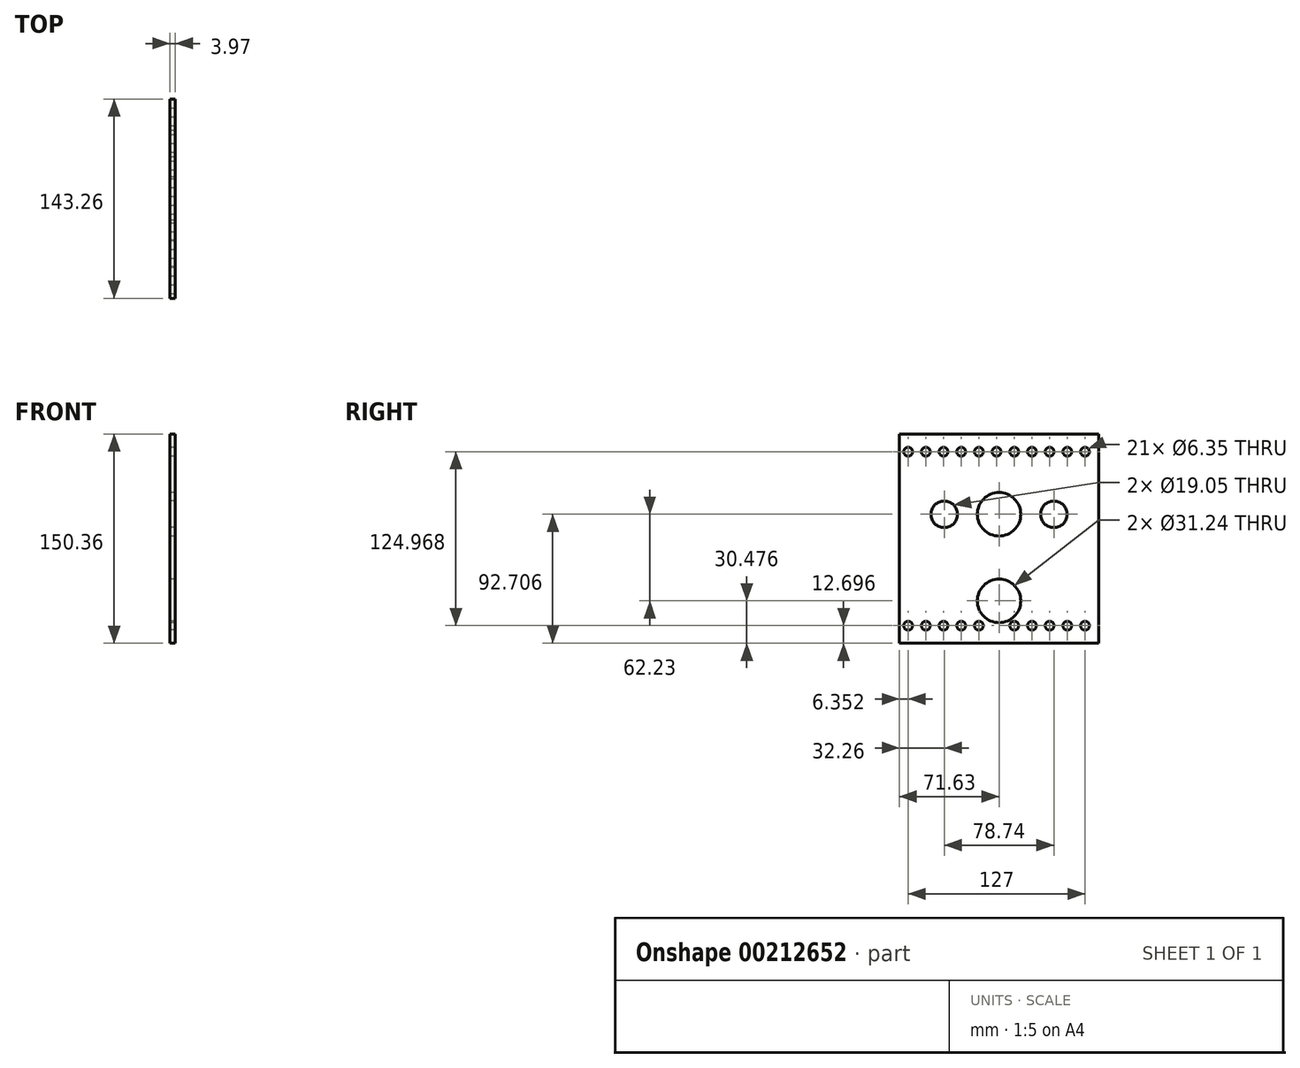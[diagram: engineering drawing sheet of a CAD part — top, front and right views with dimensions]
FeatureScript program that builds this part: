
annotation { "Feature Type Name" : "Feature", "Feature Type Description" : "" }
export const myFeature = defineFeature(function(context is Context, id is Id, definition is map)
    precondition{}
    {
        {
            var Q0;
            Q0=qCreatedBy(makeId("Right.planeOp"),FACE);
            var sketch = newSketch(context, id + "F0", { "sketchPlane" : qUnion([Q0])});
            skLineSegment(sketch, "E0.bottom", {"start": v(71.63, 75.18) * mm, "end": v(-71.63, 75.18) * mm});
            skLineSegment(sketch, "E0.top", {"start": v(71.63, -75.18) * mm, "end": v(-71.63, -75.18) * mm});
            skLineSegment(sketch, "E0.left", {"start": v(71.63, 75.18) * mm, "end": v(71.63, -75.18) * mm});
            skLineSegment(sketch, "E0.right", {"start": v(-71.63, 75.18) * mm, "end": v(-71.63, -75.18) * mm});
            skPoint(sketch, "E0.middle", {"position": v(0, 0) * mm});
            skLineSegment(sketch, "E1", {"start": v(-71.63, 49.78) * mm, "end": v(71.63, 49.78) * mm, "construction": true});
            skLineSegment(sketch, "E2", {"start": v(-71.63, -49.78) * mm, "end": v(71.63, -49.78) * mm, "construction": true});
            skCircle(sketch, "E3", {"center": v(-39.37, 17.53) * mm, "radius": 7.62 * mm, "construction": true});
            skCircle(sketch, "E4", {"center": v(39.37, 17.53) * mm, "radius": 7.62 * mm, "construction": true});
            skLineSegment(sketch, "E5", {"start": v(-39.37, 17.53) * mm, "end": v(-71.63, 17.53) * mm, "construction": true});
            skLineSegment(sketch, "E6", {"start": v(39.37, 17.53) * mm, "end": v(71.63, 17.53) * mm, "construction": true});
            skCircle(sketch, "E7", {"center": v(0, 17.53) * mm, "radius": 31.75 * mm, "construction": true});
            skCircle(sketch, "E8", {"center": v(-39.37, 17.53) * mm, "radius": 32.26 * mm, "construction": true});
            skCircle(sketch, "E9", {"center": v(39.37, 17.53) * mm, "radius": 32.26 * mm, "construction": true});
            skCircle(sketch, "E10", {"center": v(0, -44.7) * mm, "radius": 50.8 * mm, "construction": true});
            skPoint(sketch, "E10.centerSnap0", {"position": v(0, -49.78) * mm});
            skCircle(sketch, "E11", {"center": v(0, -44.7) * mm, "radius": 15.62 * mm});
            skLineSegment(sketch, "E12", {"start": v(0, -44.7) * mm, "end": v(0, -75.18) * mm, "construction": true});
            skCircle(sketch, "E13", {"center": v(0, 17.53) * mm, "radius": 15.62 * mm});
            skCircle(sketch, "E14", {"center": v(-39.37, 17.53) * mm, "radius": 9.53 * mm});
            skCircle(sketch, "E15", {"center": v(39.37, 17.53) * mm, "radius": 9.53 * mm});
            skCircle(sketch, "E16", {"center": v(0, 17.53) * mm, "radius": 8.9 * mm, "construction": true});
            skCircle(sketch, "E17", {"center": v(0, -44.7) * mm, "radius": 53.34 * mm, "construction": true});
            skLineSegment(sketch, "E18", {"start": v(-71.63, 62.48) * mm, "end": v(71.63, 62.48) * mm, "construction": true});
            skCircle(sketch, "E19", {"center": v(-65.28, 62.48) * mm, "radius": 3.18 * mm});
            skCircle(sketch, "E20.1.0.0", {"center": v(-52.58, 62.48) * mm, "radius": 3.18 * mm});
            skCircle(sketch, "E20.2.0.0", {"center": v(-39.88, 62.48) * mm, "radius": 3.18 * mm});
            skCircle(sketch, "E20.3.0.0", {"center": v(-27.18, 62.48) * mm, "radius": 3.18 * mm});
            skCircle(sketch, "E20.4.0.0", {"center": v(-14.48, 62.48) * mm, "radius": 3.18 * mm});
            skCircle(sketch, "E20.5.0.0", {"center": v(-1.78, 62.48) * mm, "radius": 3.18 * mm});
            skCircle(sketch, "E20.6.0.0", {"center": v(10.92, 62.48) * mm, "radius": 3.18 * mm});
            skCircle(sketch, "E20.7.0.0", {"center": v(23.62, 62.48) * mm, "radius": 3.18 * mm});
            skCircle(sketch, "E20.8.0.0", {"center": v(36.32, 62.48) * mm, "radius": 3.18 * mm});
            skCircle(sketch, "E20.9.0.0", {"center": v(49.02, 62.48) * mm, "radius": 3.18 * mm});
            skCircle(sketch, "E20.10.0.0", {"center": v(61.72, 62.48) * mm, "radius": 3.18 * mm});
            skLineSegment(sketch, "E20.direction1", {"start": v(-65.28, 62.48) * mm, "end": v(-52.58, 62.48) * mm, "construction": true});
            skLineSegment(sketch, "E21", {"start": v(0, 0) * mm, "end": v(-165.9, 0) * mm, "construction": true});
            skCircle(sketch, "E22.MirrorC", {"center": v(61.72, -62.48) * mm, "radius": 3.18 * mm});
            skCircle(sketch, "E23.MirrorC", {"center": v(49.02, -62.48) * mm, "radius": 3.18 * mm});
            skCircle(sketch, "E24.MirrorC", {"center": v(36.32, -62.48) * mm, "radius": 3.18 * mm});
            skCircle(sketch, "E25.MirrorC", {"center": v(23.62, -62.48) * mm, "radius": 3.18 * mm});
            skCircle(sketch, "E26.MirrorC", {"center": v(10.92, -62.48) * mm, "radius": 3.18 * mm});
            skCircle(sketch, "E27.MirrorC", {"center": v(-14.48, -62.48) * mm, "radius": 3.18 * mm});
            skCircle(sketch, "E28.MirrorC", {"center": v(-27.18, -62.48) * mm, "radius": 3.18 * mm});
            skCircle(sketch, "E29.MirrorC", {"center": v(-39.88, -62.48) * mm, "radius": 3.18 * mm});
            skCircle(sketch, "E30.MirrorC", {"center": v(-52.58, -62.48) * mm, "radius": 3.18 * mm});
            skCircle(sketch, "E31.MirrorC", {"center": v(-65.28, -62.48) * mm, "radius": 3.18 * mm});
            skSolve(sketch);
        }
        {
            var Q0;
            Q0=makeQuery(id+"F0.imprint","IMPRINT",FACE,{"disambiguationData":[TD([[makeQuery(id+"F0.imprint","IMPRINT",EDGE,{"derivedFrom":sQuery(id+"F0.wireOp",EDGE,"E0.bottom")}),1.0]])]});
            extrude(context, id + "F1", {"entities" : qUnion([Q0]), "depth" : 3.97 * mm});
        }
    });
